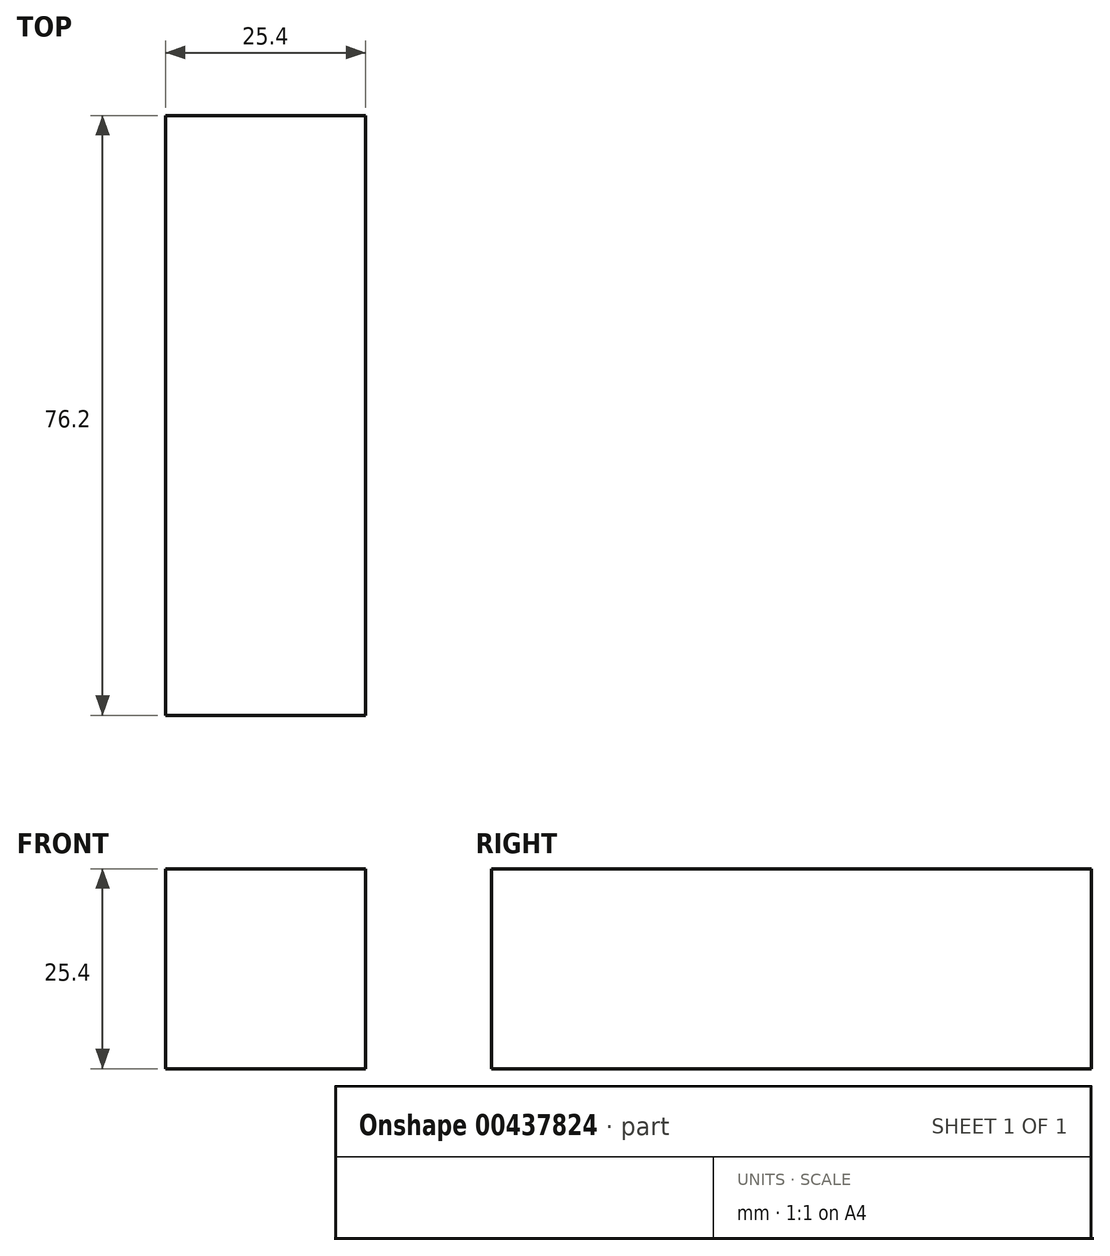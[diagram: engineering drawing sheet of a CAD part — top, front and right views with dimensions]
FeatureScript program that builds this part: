
annotation { "Feature Type Name" : "Feature", "Feature Type Description" : "" }
export const myFeature = defineFeature(function(context is Context, id is Id, definition is map)
    precondition{}
    {
        {
            var Q0;
            Q0=qCreatedBy(makeId("Front.planeOp"),FACE);
            var sketch = newSketch(context, id + "F0", { "sketchPlane" : qUnion([Q0])});
            skLineSegment(sketch, "E0.bottom", {"start": v(-12.7, 12.7) * mm, "end": v(12.7, 12.7) * mm});
            skLineSegment(sketch, "E0.top", {"start": v(-12.7, -12.7) * mm, "end": v(12.7, -12.7) * mm});
            skLineSegment(sketch, "E0.left", {"start": v(-12.7, 12.7) * mm, "end": v(-12.7, -12.7) * mm});
            skLineSegment(sketch, "E0.right", {"start": v(12.7, 12.7) * mm, "end": v(12.7, -12.7) * mm});
            skPoint(sketch, "E0.middle", {"position": v(0, 0) * mm});
            skSolve(sketch);
        }
        {
            var Q0;
            Q0 = qSketchRegion(id + "F0", true);
            extrude(context, id + "F1", {"entities" : qUnion([Q0]), "depth" : 76.2 * mm});
        }
    });
